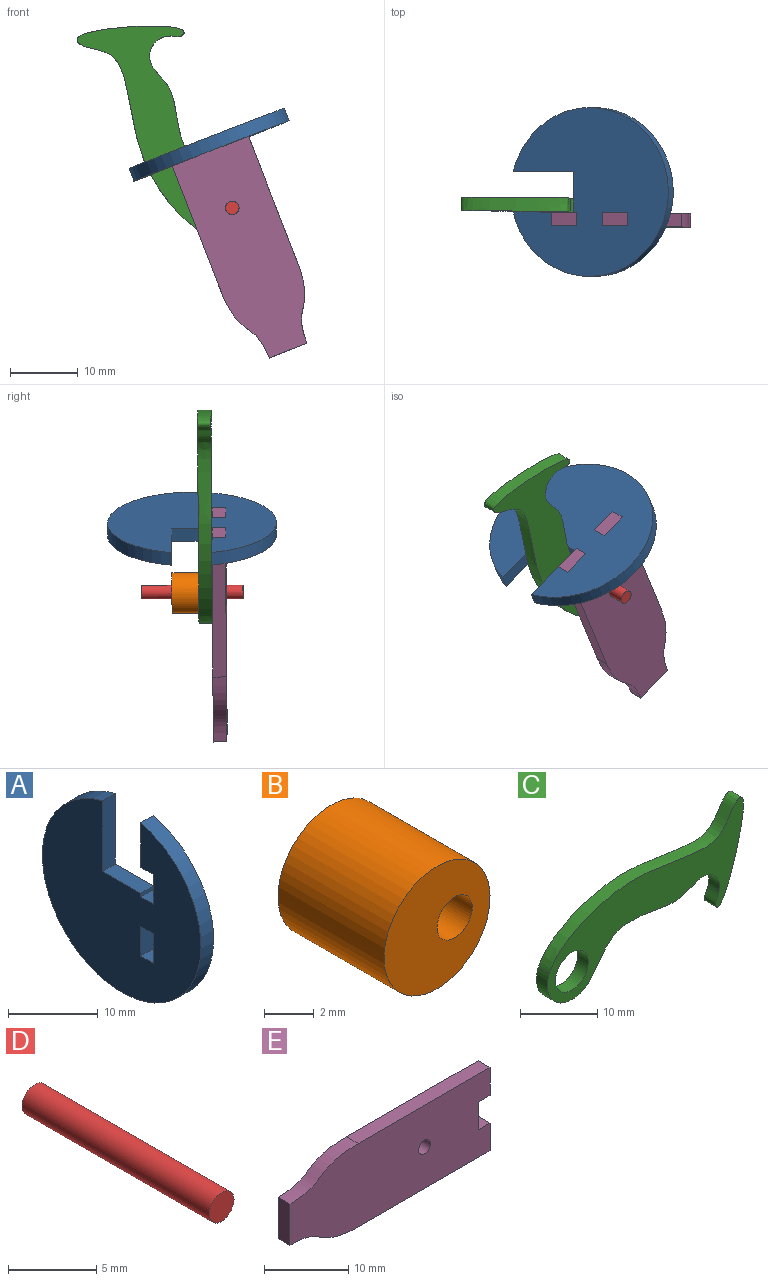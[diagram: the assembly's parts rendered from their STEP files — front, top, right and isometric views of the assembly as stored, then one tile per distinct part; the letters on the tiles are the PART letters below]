
ASSEMBLY  parts=5 mates=4
PART A: 14 faces, bbox 2x25x24.6 mm
  f0: plane 6.08x2mm, normal (0,1,0), area 12.2mm2, adj f1,f2,f5,f10
  f1: plane 25x24.63mm, normal (-1,0,0), area 415.4mm2, adj f0,f3,f4,f5,f6,f7,f8,f9
  f2: plane 25x24.63mm, normal (1,0,0), area 415.4mm2, adj f0,f3,f4,f5,f6,f7,f8,f9
  f3: plane 9.63x2mm, normal (0,-1,0), area 19.3mm2, adj f1,f2,f4,f5
  f4: plane 6x2mm, normal (0,0,1), area 12mm2, adj f1,f2,f3,f12
  f5: cylinder r=12.5mm len=25mm, axis (1,0,0), area 145mm2, adj f0,f1,f2,f3
  f6: plane 4.04x2mm, normal (0,1,0), area 8.1mm2, adj f1,f2,f8,f9
  f7: plane 4.04x2mm, normal (0,-1,0), area 8.1mm2, adj f1,f2,f8,f9
  f8: plane 2x2mm, normal (0,0,-1), area 4mm2, adj f1,f2,f6,f7
  f9: plane 2x2mm, normal (0,0,1), area 4mm2, adj f1,f2,f6,f7
  f10: plane 2x2mm, normal (0,0,-1), area 4mm2, adj f0,f1,f2,f11
  f11: plane 4.04x2mm, normal (0,1,0), area 8.1mm2, adj f1,f2,f10,f13
  f12: plane 2x0.48mm, normal (0,-1,0), area 1mm2, adj f1,f2,f4,f13
  f13: plane 2x2mm, normal (0,0,1), area 4mm2, adj f1,f2,f11,f12
PART B: 4 faces, bbox 6x6x6 mm
  f0: cylinder r=1mm len=6mm, axis (0,1,0), area 37.7mm2, adj f2,f3
  f1: cylinder r=3mm len=6mm, axis (0,1,0), area 113.1mm2, adj f2,f3
  f2: plane 6x6mm, normal (0,-1,0), area 25.1mm2, adj f0,f1
  f3: plane 6x6mm, normal (0,1,0), area 25.1mm2, adj f0,f1
PART C: 9 faces, bbox 36.8x2x17.2 mm
  f0: plane 2x2mm, normal (0,0,-1), area 4mm2, adj f1,f5,f7,f8
  f1: extruded ~11.01x2mm, area 22.5mm2, adj f0,f2,f7,f8
  f2: cylinder r=3mm len=3.99mm, axis (0,1,0), area 13mm2, adj f1,f3,f7,f8
  f3: extruded ~35.53x15.25mm, area 117mm2, adj f2,f4,f7,f8
  f4: cylinder r=4.5mm len=6.99mm, axis (0,1,0), area 22.9mm2, adj f3,f5,f7,f8
  f5: extruded ~7.51x6.25mm, area 20.2mm2, adj f0,f4,f7,f8
  f6: cylinder r=3mm len=6mm, axis (0,1,0), area 37.7mm2, adj f7,f8
  f7: plane 36.76x17.23mm, normal (0,-1,0), area 232.4mm2, adj f0,f1,f2,f3,f4,f5,f6
  f8: plane 36.76x17.23mm, normal (0,1,0), area 232.4mm2, adj f0,f1,f2,f3,f4,f5,f6
PART D: 3 faces, bbox 2x15x2 mm
  f0: cylinder r=1mm len=15mm, axis (0,1,0), area 94.2mm2, adj f1,f2
  f1: plane 2x2mm, normal (0,-1,0), area 3.1mm2, adj f0
  f2: plane 2x2mm, normal (0,1,0), area 3.1mm2, adj f0
PART E: 13 faces, bbox 33.7x2x12.1 mm
  f0: plane 6x2mm, normal (-1,0,0), area 12mm2, adj f1,f10,f11,f12
  f1: extruded ~11.51x3.06mm, area 24.2mm2, adj f0,f2,f11,f12
  f2: plane 22.15x2mm, normal (0,0,-1), area 44.3mm2, adj f1,f3,f11,f12
  f3: plane 4.04x2mm, normal (1,0,0), area 8.1mm2, adj f2,f4,f11,f12
  f4: plane 2x2mm, normal (0,0,1), area 4mm2, adj f3,f5,f11,f12
  f5: plane 4.04x2mm, normal (1,0,0), area 8.1mm2, adj f4,f6,f11,f12
  f6: plane 2x2mm, normal (0,0,-1), area 4mm2, adj f5,f7,f11,f12
  f7: plane 4.04x2mm, normal (1,0,0), area 8.1mm2, adj f6,f8,f11,f12
  f8: plane 22.15x2mm, normal (0,0,1), area 44.3mm2, adj f7,f10,f11,f12
  f9: cylinder r=1mm len=2mm, axis (0,1,0), area 12.6mm2, adj f11,f12
  f10: extruded ~11.51x3.06mm, area 24.2mm2, adj f0,f8,f11,f12
  f11: plane 33.66x12.12mm, normal (0,-1,0), area 363.2mm2, adj f0,f1,f2,f3,f4,f5,f6,f7
  f12: plane 33.66x12.12mm, normal (0,1,0), area 363.2mm2, adj f0,f1,f2,f3,f4,f5,f6,f7
PLACE A rot(axis=(0,-1,0),111.3deg) t=(-21.74,-3.89,14.83)mm
PLACE B rot(axis=(-0.03,-1,-0.05),6.4deg) t=(-1.04,-4.06,2.31)mm
PLACE C rot(axis=(0,-1,0),109.8deg) t=(-22.84,-4.86,15.79)mm
PLACE D rot(axis=(-0.03,-1,-0.05),6.4deg) t=(-1.04,-4.06,2.31)mm
PLACE E rot(axis=(0,-1,0),111.3deg) t=(-21.74,-3.89,14.83)mm fixed
MATE revolute D.f0 <-> E.f9  axis (0.01,1,0) through (-16.25,-11.47,0.64)mm
MATE fastened A.f2 <-> E.f3  axis (-0.36,0.01,0.93) through (-14.58,-7.94,13.08)mm
MATE fastened D.f0 <-> B.f0  axis (0.01,1,0) through (-16.16,3.53,0.59)mm
MATE cylindrical B.f3 <-> C.f4  axis (0.01,1,0) through (-17.3,-0.97,0.48)mm
